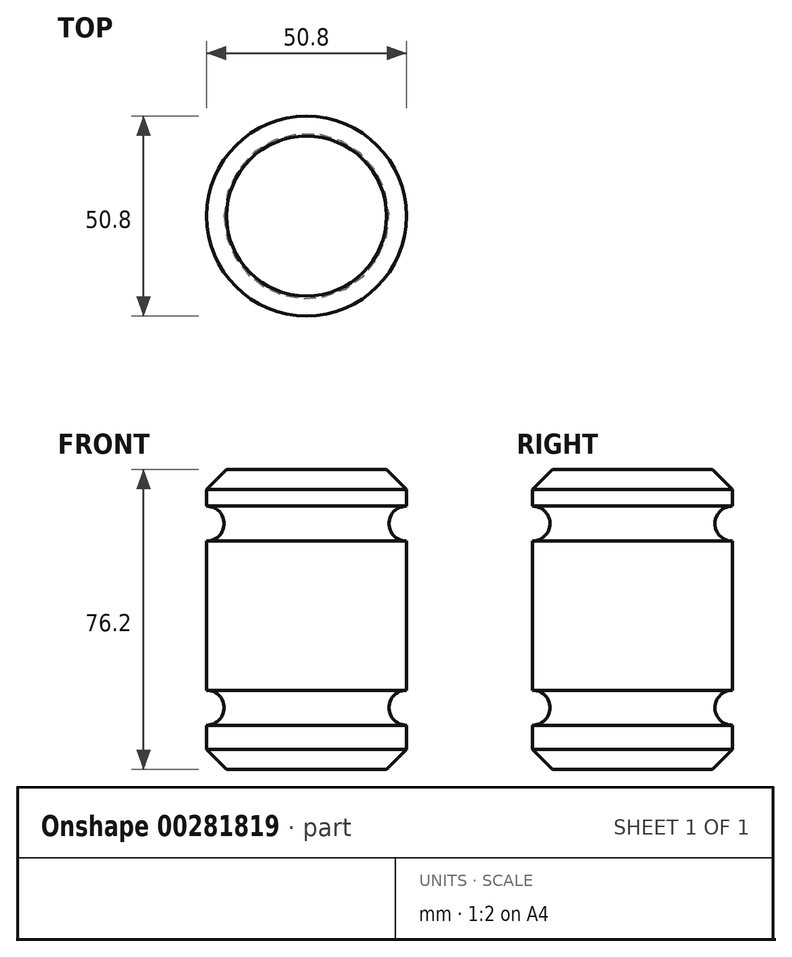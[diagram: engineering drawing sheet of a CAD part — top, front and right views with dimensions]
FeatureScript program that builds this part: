
annotation { "Feature Type Name" : "Feature", "Feature Type Description" : "" }
export const myFeature = defineFeature(function(context is Context, id is Id, definition is map)
    precondition{}
    {
        {
            var Q0;
            Q0=qCreatedBy(makeId("Front.planeOp"),FACE);
            var sketch = newSketch(context, id + "F0", { "sketchPlane" : qUnion([Q0])});
            skLineSegment(sketch, "E0.bottom", {"start": v(0, 0) * mm, "end": v(-25.4, 0) * mm});
            skLineSegment(sketch, "E0.top", {"start": v(0, 76.2) * mm, "end": v(-25.4, 76.2) * mm});
            skLineSegment(sketch, "E0.left", {"start": v(0, 0) * mm, "end": v(0, 11.24) * mm});
            skLineSegment(sketch, "E0.right", {"start": v(-25.4, 0) * mm, "end": v(-25.4, 76.2) * mm});
            skArc(sketch, "E1", {"start": v(0, 66.9) * mm, "mid": v(-4.45, 62.45) * mm, "end": v(0, 58) * mm});
            skArc(sketch, "E2", {"start": v(0, 20.13) * mm, "mid": v(-4.45, 15.69) * mm, "end": v(0, 11.24) * mm});
            skLineSegment(sketch, "E3.trimOffspring", {"start": v(0, 66.9) * mm, "end": v(0, 76.2) * mm});
            skLineSegment(sketch, "E4.trimOffspring", {"start": v(0, 20.13) * mm, "end": v(0, 58) * mm});
            skSolve(sketch);
        }
        {
            var Q0;
            Q0=makeQuery(id+"F0.imprint","IMPRINT",FACE,{"disambiguationData":[TD([[makeQuery(id+"F0.imprint","IMPRINT",EDGE,{"derivedFrom":sQuery(id+"F0.wireOp",EDGE,"E0.bottom")}),-1.0]])]});
            var Q1;
            Q1=sQuery(id+"F0.wireOp",EDGE,"E0.right");
            revolve(context, id + "F1", {"entities" : qUnion([Q0]), "axis" : qUnion([Q1]), "revolveType" : RevolveType.FULL});
        }
        {
            var Q0;
            Q0=makeQuery(id+"F1.opRevolve","SWEPT_EDGE",EDGE,{"disambiguationData":[OSD([sQuery(id+"F0.wireOp",EDGE,"E0.bottom"),sQuery(id+"F0.wireOp",EDGE,"E0.left")])]});
            var Q1;
            Q1=makeQuery(id+"F1.opRevolve","SWEPT_EDGE",EDGE,{"disambiguationData":[OSD([sQuery(id+"F0.wireOp",EDGE,"E0.top"),sQuery(id+"F0.wireOp",EDGE,"E3.trimOffspring")])]});
            chamfer(context, id + "F2", {"entities" : qUnion([Q0, Q1]), "width" : 5.08 * mm, "tangentPropagation" : true});
        }
    });
